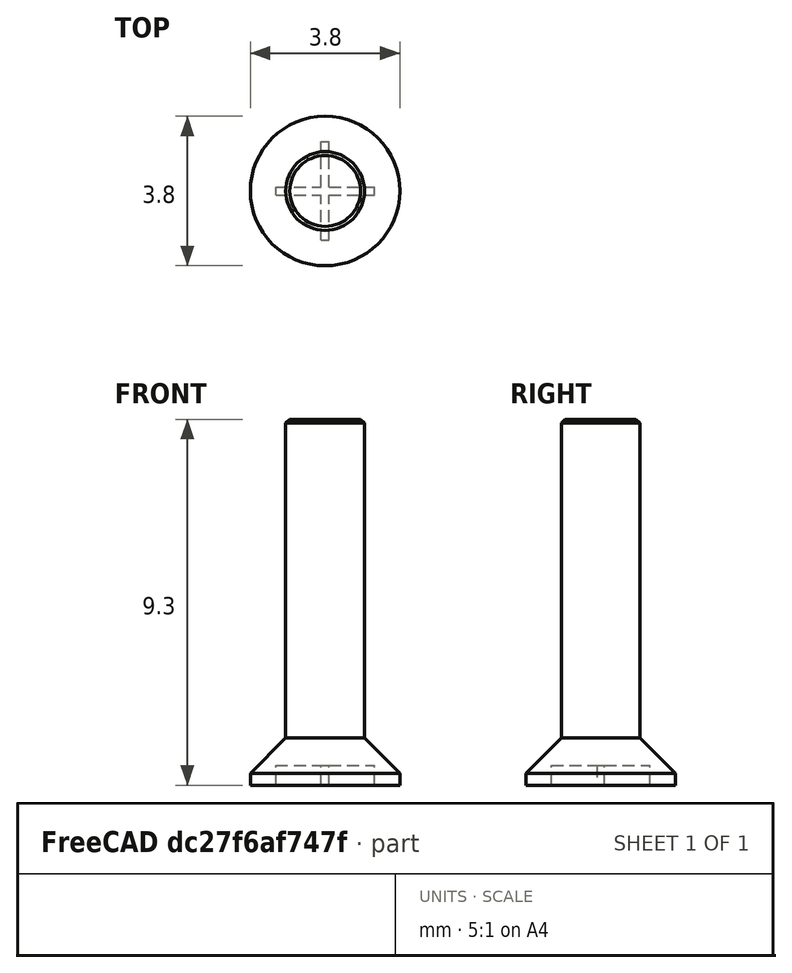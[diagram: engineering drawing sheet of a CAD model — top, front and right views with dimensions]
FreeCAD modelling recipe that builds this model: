
FCSTD DOCUMENT  (FreeCAD 0.16R6706 (Git))
Label: Screw_M2
License: All rights reserved
LicenseURL: http://en.wikipedia.org/wiki/All_rights_reserved
objects: Part::Cylinder×2, Part::Box×2, Part::MultiFuse×2, PartDesign::Chamfer×2, Part::Cut×1
note: 9 computed .brp shape members not serialized (recipe doc carries the construction recipe); baked Part::Feature solids carry a one-line shape summary decoded from their .brp

FEATURE [Part::Cylinder] Cylinder  label="Zylinder"
  Angle = 360
  Height = 1.2
  Radius = 1.9
FEATURE [Part::Cylinder] Cylinder001  label="Zylinder001"
  Angle = 360
  Height = 9.2
  Placement = pos=(0,0,0.1) rot=(0,0,1;0rad)
  Radius = 1
FEATURE [Part::Box] Box  label="Würfel"
  Height = 0.5
  Length = 0.2
  Placement = pos=(-0.1,-1.25,0) rot=(0,0,1;0rad)
  Width = 2.5
FEATURE [Part::Box] Box001  label="Würfel001"
  Height = 0.5
  Length = 2.5
  Placement = pos=(-1.25,-0.1,0) rot=(0,0,1;0rad)
  Width = 0.2
FEATURE [Part::MultiFuse] Fusion
  Shapes = -> [Box001,Box]
FEATURE [Part::MultiFuse] Fusion001
  Shapes = -> [Cylinder001,Cylinder]
FEATURE [Part::Cut] Cut
  Base = -> Fusion001
  Tool = -> Fusion
FEATURE [PartDesign::Chamfer] Chamfer
  Base = -> Cut [Edge4]
  Size = 0.8999
FEATURE [PartDesign::Chamfer] Chamfer001  label="SCREW"
  Base = -> Chamfer [Edge6]
  Size = 0.1
